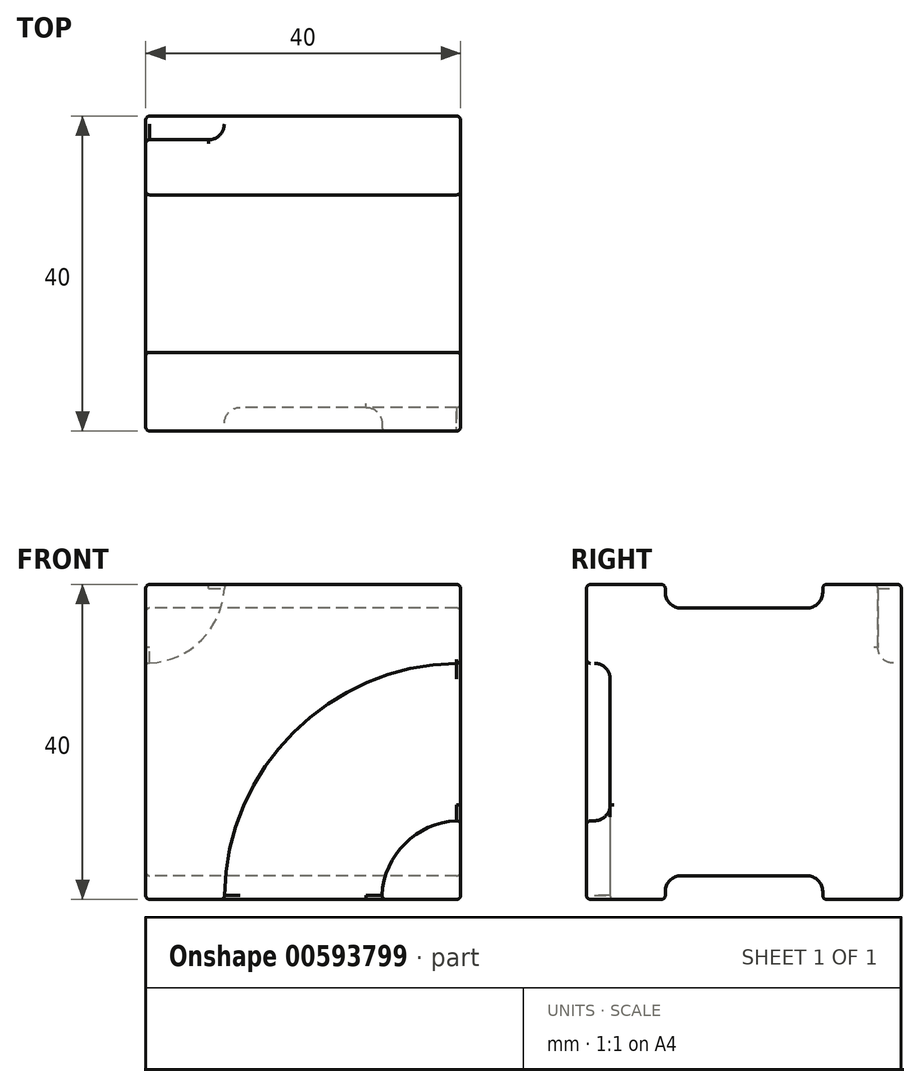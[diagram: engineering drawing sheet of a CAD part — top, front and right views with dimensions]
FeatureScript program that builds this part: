
annotation { "Feature Type Name" : "Feature", "Feature Type Description" : "" }
export const myFeature = defineFeature(function(context is Context, id is Id, definition is map)
    precondition{}
    {
        {
            var Q0;
            Q0=qCreatedBy(makeId("Front.planeOp"),FACE);
            var sketch = newSketch(context, id + "F0", { "sketchPlane" : qUnion([Q0])});
            skLineSegment(sketch, "E0.bottom", {"start": v(20, -20) * mm, "end": v(-20, -20) * mm});
            skLineSegment(sketch, "E0.top", {"start": v(20, 20) * mm, "end": v(-20, 20) * mm});
            skLineSegment(sketch, "E0.left", {"start": v(20, -20) * mm, "end": v(20, 20) * mm});
            skLineSegment(sketch, "E0.right", {"start": v(-20, -20) * mm, "end": v(-20, 20) * mm});
            skPoint(sketch, "E0.middle", {"position": v(0, 0) * mm});
            skSolve(sketch);
        }
        {
            var Q0;
            Q0=makeQuery(id+"F0.imprint","IMPRINT",FACE,{"disambiguationData":[TD([[makeQuery(id+"F0.imprint","IMPRINT",EDGE,{"derivedFrom":sQuery(id+"F0.wireOp",EDGE,"E0.bottom")}),-1.0]])]});
            extrude(context, id + "F1", {"entities" : qUnion([Q0]), "depth" : 40 * mm, "offsetDistance" : 25 * mm, "symmetric" : true});
        }
        {
            var Q0;
            Q0=makeQuery(id+"F1.opExtrude","SWEPT_FACE",FACE,{"disambiguationData":[OSD([sQuery(id+"F0.wireOp",EDGE,"E0.top")])]});
            var sketch = newSketch(context, id + "F2", { "sketchPlane" : qUnion([Q0])});
            skLineSegment(sketch, "E1", {"start": v(34.86, 0) * mm, "end": v(-35.2, 0) * mm, "construction": true});
            skPoint(sketch, "E1.endSnap0", {"position": v(-20, 0) * mm});
            skLineSegment(sketch, "E2.bottom", {"start": v(20, 10) * mm, "end": v(-20, 10) * mm});
            skLineSegment(sketch, "E2.right", {"start": v(-20, 10) * mm, "end": v(-20, 0) * mm});
            skLineSegment(sketch, "E3", {"start": v(20, 10) * mm, "end": v(20, 0) * mm});
            skLineSegment(sketch, "E4.MirrorCS", {"start": v(-20, -10) * mm, "end": v(-20, 0) * mm});
            skLineSegment(sketch, "E5.MirrorCS", {"start": v(20, -10) * mm, "end": v(20, 0) * mm});
            skLineSegment(sketch, "E6.MirrorCS", {"start": v(20, -10) * mm, "end": v(-20, -10) * mm});
            skSolve(sketch);
        }
        {
            var Q0;
            Q0=qSketchRegion(id+"F2",true);
            extrude(context, id + "F3", {"entities" : qUnion([Q0]), "operationType" : NewBodyOperationType.REMOVE, "oppositeDirection" : true, "depth" : 3 * mm, "offsetDistance" : 25 * mm});
        }
        {
            var Q0;
            Q0=makeQuery(id+"F1.opExtrude","SWEPT_FACE",FACE,{"disambiguationData":[OSD([sQuery(id+"F0.wireOp",EDGE,"E0.bottom")])]});
            var sketch = newSketch(context, id + "F4", { "sketchPlane" : qUnion([Q0])});
            skLineSegment(sketch, "E7", {"start": v(31.12, 0) * mm, "end": v(-32.74, 0) * mm, "construction": true});
            skPoint(sketch, "E7.endSnap0", {"position": v(24.5, 0) * mm});
            skLineSegment(sketch, "E8.bottom", {"start": v(20, 10) * mm, "end": v(-20, 10) * mm});
            skLineSegment(sketch, "E8.top", {"start": v(20, -10) * mm, "end": v(-20, -10) * mm});
            skLineSegment(sketch, "E8.left", {"start": v(20, 10) * mm, "end": v(20, -10) * mm});
            skLineSegment(sketch, "E8.right", {"start": v(-20, 10) * mm, "end": v(-20, -10) * mm});
            skSolve(sketch);
        }
        {
            var Q0;
            Q0=qSketchRegion(id+"F4",true);
            extrude(context, id + "F5", {"entities" : qUnion([Q0]), "operationType" : NewBodyOperationType.REMOVE, "oppositeDirection" : true, "depth" : 3 * mm, "offsetDistance" : 25 * mm});
        }
        {
            var Q0;
            Q0=makeQuery(id+"F1.opExtrude","CAP_FACE",FACE,{"disambiguationData":[OSD([sQuery(id+"F0.wireOp",EDGE,"E0.bottom"),sQuery(id+"F0.wireOp",EDGE,"E0.top"),sQuery(id+"F0.wireOp",EDGE,"E0.left"),sQuery(id+"F0.wireOp",EDGE,"E0.right")])],"isStart":false});
            var sketch = newSketch(context, id + "F6", { "sketchPlane" : qUnion([Q0])});
            skArc(sketch, "E9", {"start": v(10, -20) * mm, "mid": v(12.93, -12.93) * mm, "end": v(20, -10) * mm});
            skArc(sketch, "E10.0", {"start": v(-10, -20) * mm, "mid": v(-1.21, 1.21) * mm, "end": v(20, 10) * mm});
            skLineSegment(sketch, "E11", {"start": v(10, -20) * mm, "end": v(-10, -20) * mm});
            skLineSegment(sketch, "E12", {"start": v(20, -10) * mm, "end": v(20, 10) * mm});
            skSolve(sketch);
        }
        {
            var Q0;
            Q0=qSketchRegion(id+"F6",true);
            extrude(context, id + "F7", {"entities" : qUnion([Q0]), "operationType" : NewBodyOperationType.REMOVE, "oppositeDirection" : true, "depth" : 3 * mm, "offsetDistance" : 25 * mm});
        }
        {
            var Q0;
            Q0=makeQuery(id+"F1.opExtrude","CAP_FACE",FACE,{"disambiguationData":[OSD([sQuery(id+"F0.wireOp",EDGE,"E0.bottom"),sQuery(id+"F0.wireOp",EDGE,"E0.top"),sQuery(id+"F0.wireOp",EDGE,"E0.left"),sQuery(id+"F0.wireOp",EDGE,"E0.right")])],"isStart":true});
            var sketch = newSketch(context, id + "F8", { "sketchPlane" : qUnion([Q0])});
            skArc(sketch, "E13", {"start": v(20, 10) * mm, "mid": v(12.93, 12.93) * mm, "end": v(10, 20) * mm});
            skArc(sketch, "E14", {"start": v(20, -10) * mm, "mid": v(-1.21, -1.21) * mm, "end": v(-10, 20) * mm});
            skLineSegment(sketch, "E15", {"start": v(20, -10) * mm, "end": v(20, 10) * mm});
            skLineSegment(sketch, "E16", {"start": v(10, 20) * mm, "end": v(-10, 20) * mm});
            skLineSegment(sketch, "E17", {"start": v(-10, 20) * mm, "end": v(-10, -20) * mm});
            skLineSegment(sketch, "E18", {"start": v(-10, -20) * mm, "end": v(10, -20) * mm});
            skArc(sketch, "E19", {"start": v(10, -20) * mm, "mid": v(12.93, -12.93) * mm, "end": v(20, -10) * mm});
            skSolve(sketch);
        }
        {
            var Q0;
            Q0=makeQuery(id+"F8.imprint","IMPRINT",FACE,{"disambiguationData":[TD([[makeQuery(id+"F8.imprint","IMPRINT",EDGE,{"derivedFrom":sQuery(id+"F8.wireOp",EDGE,"S0vOXXMj-KSPf-uTmC-3DLV-lmScbWxBIAN8")}),1.0]])]});
            var Q1;
            Q1=makeQuery(id+"F8.imprint","IMPRINT",FACE,{"disambiguationData":[TD([[makeQuery(id+"F8.imprint","IMPRINT",EDGE,{"derivedFrom":sQuery(id+"F8.wireOp",EDGE,"E13")}),1.0]])]});
            extrude(context, id + "F9", {"entities" : qUnion([Q0, Q1]), "operationType" : NewBodyOperationType.REMOVE, "oppositeDirection" : true, "depth" : 3 * mm, "offsetDistance" : 25 * mm});
        }
        {
            var Q0;
            Q0=makeQuery(id+"F5.boolean.opBoolean","COPY",EDGE,{"derivedFrom":makeQuery(id+"F5.opExtrude","CAP_EDGE",EDGE,{"disambiguationData":[OSD([sQuery(id+"F4.wireOp",EDGE,"E8.top")])],"isStart":false})});
            var Q1;
            Q1=makeQuery(id+"F5.boolean.opBoolean","COPY",EDGE,{"derivedFrom":makeQuery(id+"F5.opExtrude","CAP_EDGE",EDGE,{"disambiguationData":[OSD([sQuery(id+"F4.wireOp",EDGE,"E8.bottom")])],"isStart":false})});
            var Q2;
            Q2=makeQuery(id+"F7.boolean.opBoolean","COPY",EDGE,{"derivedFrom":makeQuery(id+"F7.opExtrude","CAP_EDGE",EDGE,{"disambiguationData":[OSD([sQuery(id+"F6.wireOp",EDGE,"E10.0")])],"isStart":false})});
            var Q3;
            Q3=makeQuery(id+"F7.boolean.opBoolean","COPY",EDGE,{"derivedFrom":makeQuery(id+"F7.opExtrude","CAP_EDGE",EDGE,{"disambiguationData":[OSD([sQuery(id+"F6.wireOp",EDGE,"E9")])],"isStart":false})});
            var Q4;
            Q4=makeQuery(id+"F9.boolean.opBoolean","COPY",EDGE,{"derivedFrom":makeQuery(id+"F9.opExtrude","CAP_EDGE",EDGE,{"disambiguationData":[OSD([sQuery(id+"F8.wireOp",EDGE,"E17")])],"isStart":false})});
            var Q5;
            Q5=makeQuery(id+"F9.boolean.opBoolean","COPY",EDGE,{"derivedFrom":makeQuery(id+"F9.opExtrude","CAP_EDGE",EDGE,{"disambiguationData":[OSD([sQuery(id+"F8.wireOp",EDGE,"E13")])],"isStart":false})});
            var Q6;
            Q6=makeQuery(id+"F9.boolean.opBoolean","COPY",EDGE,{"derivedFrom":makeQuery(id+"F9.opExtrude","CAP_EDGE",EDGE,{"disambiguationData":[OSD([sQuery(id+"F8.wireOp",EDGE,"E19")])],"isStart":false})});
            var Q7;
            Q7=makeQuery(id+"F3.boolean.opBoolean","COPY",EDGE,{"derivedFrom":makeQuery(id+"F3.opExtrude","CAP_EDGE",EDGE,{"disambiguationData":[OSD([sQuery(id+"F2.wireOp",EDGE,"E6.MirrorCS")])],"isStart":false})});
            var Q8;
            Q8=makeQuery(id+"F3.boolean.opBoolean","COPY",EDGE,{"derivedFrom":makeQuery(id+"F3.opExtrude","CAP_EDGE",EDGE,{"disambiguationData":[OSD([sQuery(id+"F2.wireOp",EDGE,"E2.bottom")])],"isStart":false})});
            var Q9;
            Q9=makeQuery(id+"F9.boolean.opBoolean","COPY",EDGE,{"derivedFrom":makeQuery(id+"F9.opExtrude","CAP_EDGE",EDGE,{"disambiguationData":[OSD([sQuery(id+"F8.wireOp",EDGE,"E14")])],"isStart":false})});
            fillet(context, id + "F10", {"entities" : qUnion([Q0, Q1, Q2, Q3, Q4, Q5, Q6, Q7, Q8, Q9]), "radius" : 2 * mm, "tangentPropagation" : true, "allowEdgeOverflow" : false});
        }
        {
            var Q0;
            {var subQ0=sQuery(id+"F0.wireOp",EDGE,"E0.left");var subQ1=sQuery(id+"F0.wireOp",EDGE,"E0.top");var subQ2=sQuery(id+"F0.wireOp",EDGE,"E0.right");var subQ5=sQuery(id+"F0.wireOp",EDGE,"E0.bottom");Q0=makeQuery(id+"FeEYurADESSjoWS_1.boolean.opBoolean","SPLIT",FACE,{"disambiguationData":[TD([makeQuery(id+"F1.opExtrude","SWEPT_FACE",FACE,{"disambiguationData":[OSD([subQ1])]})])],"derivedFrom":makeQuery(id+"F1.opExtrude","CAP_FACE",FACE,{"disambiguationData":[OSD([subQ5,subQ1,subQ0,subQ2])],"isStart":false})});}
            var Q1;
            Q1=makeQuery(id+"F1.opExtrude","SWEPT_FACE",FACE,{"disambiguationData":[OSD([sQuery(id+"F0.wireOp",EDGE,"E0.right")])]});
            var Q2;
            {var subQ0=sQuery(id+"F0.wireOp",EDGE,"E0.right");var subQ1=sQuery(id+"F0.wireOp",EDGE,"E0.bottom");Q2=makeQuery(id+"FeEYurADESSjoWS_1.boolean.opBoolean","SPLIT",FACE,{"disambiguationData":[TD([makeQuery(id+"FeEYurADESSjoWS_1.opExtrude","SWEPT_FACE",FACE,{"disambiguationData":[OSD([sQuery(id+"F6.wireOp",EDGE,"bcd692f1-bbfa-4d88-a7f8-9c818706eb5d.0")])]})])],"derivedFrom":makeQuery(id+"F1.opExtrude","CAP_FACE",FACE,{"disambiguationData":[OSD([subQ1,sQuery(id+"F0.wireOp",EDGE,"E0.top"),sQuery(id+"F0.wireOp",EDGE,"E0.left"),subQ0])],"isStart":false})});}
            var Q3;
            {var subQ2=sQuery(id+"F0.wireOp",EDGE,"E0.bottom");Q3=makeQuery(id+"F5.boolean.opBoolean","SPLIT",FACE,{"disambiguationData":[TD([makeQuery(id+"F5.opExtrude","SWEPT_FACE",FACE,{"disambiguationData":[OSD([sQuery(id+"F4.wireOp",EDGE,"E8.bottom")])]})])],"derivedFrom":makeQuery(id+"F1.opExtrude","SWEPT_FACE",FACE,{"disambiguationData":[OSD([subQ2])]})});}
            var Q4;
            {var subQ2=sQuery(id+"F0.wireOp",EDGE,"E0.bottom");Q4=makeQuery(id+"F5.boolean.opBoolean","SPLIT",FACE,{"disambiguationData":[TD([makeQuery(id+"F5.opExtrude","SWEPT_FACE",FACE,{"disambiguationData":[OSD([sQuery(id+"F4.wireOp",EDGE,"E8.top")])]})])],"derivedFrom":makeQuery(id+"F1.opExtrude","SWEPT_FACE",FACE,{"disambiguationData":[OSD([subQ2])]})});}
            var Q5;
            {var subQ0=sQuery(id+"F0.wireOp",EDGE,"E0.left");var subQ1=sQuery(id+"F0.wireOp",EDGE,"E0.top");var subQ2=sQuery(id+"F0.wireOp",EDGE,"E0.right");var subQ5=sQuery(id+"F0.wireOp",EDGE,"E0.bottom");Q5=makeQuery(id+"FHPeFrndoI6grQq_1.boolean.opBoolean","SPLIT",FACE,{"disambiguationData":[TD([makeQuery(id+"F1.opExtrude","SWEPT_FACE",FACE,{"disambiguationData":[OSD([subQ1])]})])],"derivedFrom":makeQuery(id+"F1.opExtrude","CAP_FACE",FACE,{"disambiguationData":[OSD([subQ5,subQ1,subQ0,subQ2])],"isStart":true})});}
            var Q6;
            {var subQ0=sQuery(id+"F0.wireOp",EDGE,"E0.left");var subQ1=sQuery(id+"F0.wireOp",EDGE,"E0.bottom");Q6=makeQuery(id+"FHPeFrndoI6grQq_1.boolean.opBoolean","SPLIT",FACE,{"disambiguationData":[TD([makeQuery(id+"FHPeFrndoI6grQq_1.opExtrude","SWEPT_FACE",FACE,{"disambiguationData":[OSD([sQuery(id+"FpqyqDqQfxwQ36t_1.wireOp",EDGE,"11a5f918-374d-4318-88e4-5ad5a2d605e7.0")])]})])],"derivedFrom":makeQuery(id+"F1.opExtrude","CAP_FACE",FACE,{"disambiguationData":[OSD([subQ1,sQuery(id+"F0.wireOp",EDGE,"E0.top"),subQ0,sQuery(id+"F0.wireOp",EDGE,"E0.right")])],"isStart":true})});}
            var Q7;
            {var subQ0=sQuery(id+"F0.wireOp",EDGE,"E0.left");Q7=makeQuery(id+"FhphGXGLthVadN0_1.boolean.opBoolean","SPLIT",FACE,{"disambiguationData":[TD([makeQuery(id+"F5.boolean.opBoolean","COPY",FACE,{"derivedFrom":makeQuery(id+"F5.opExtrude","SWEPT_FACE",FACE,{"disambiguationData":[OSD([sQuery(id+"F4.wireOp",EDGE,"E8.top")])]})})])],"derivedFrom":makeQuery(id+"F1.opExtrude","SWEPT_FACE",FACE,{"disambiguationData":[OSD([subQ0])]})});}
            var Q8;
            {var subQ0=sQuery(id+"F0.wireOp",EDGE,"E0.top");var subQ2=sQuery(id+"F0.wireOp",EDGE,"E0.left");Q8=makeQuery(id+"FhphGXGLthVadN0_1.boolean.opBoolean","SPLIT",FACE,{"disambiguationData":[TD([makeQuery(id+"F1.opExtrude","SWEPT_FACE",FACE,{"disambiguationData":[OSD([subQ0])]})])],"derivedFrom":makeQuery(id+"F1.opExtrude","SWEPT_FACE",FACE,{"disambiguationData":[OSD([subQ2])]})});}
            var Q9;
            {var subQ0=sQuery(id+"F0.wireOp",EDGE,"E0.left");Q9=makeQuery(id+"FhphGXGLthVadN0_1.boolean.opBoolean","SPLIT",FACE,{"disambiguationData":[TD([makeQuery(id+"F5.boolean.opBoolean","COPY",FACE,{"derivedFrom":makeQuery(id+"F5.opExtrude","SWEPT_FACE",FACE,{"disambiguationData":[OSD([sQuery(id+"F4.wireOp",EDGE,"E8.bottom")])]})})])],"derivedFrom":makeQuery(id+"F1.opExtrude","SWEPT_FACE",FACE,{"disambiguationData":[OSD([subQ0])]})});}
            var Q10;
            {var subQ1=sQuery(id+"F0.wireOp",EDGE,"E0.left");var subQ2=sQuery(id+"F0.wireOp",EDGE,"E0.top");Q10=makeQuery(id+"F3.boolean.opBoolean","SPLIT",FACE,{"disambiguationData":[TD([makeQuery(id+"F1.opExtrude","SWEPT_FACE",FACE,{"disambiguationData":[OSD([subQ1])]})])],"derivedFrom":makeQuery(id+"F1.opExtrude","SWEPT_FACE",FACE,{"disambiguationData":[OSD([subQ2])]})});}
            var Q11;
            {var subQ0=sQuery(id+"F0.wireOp",EDGE,"E0.right");var subQ2=sQuery(id+"F0.wireOp",EDGE,"E0.top");Q11=makeQuery(id+"F3.boolean.opBoolean","SPLIT",FACE,{"disambiguationData":[TD([makeQuery(id+"F1.opExtrude","SWEPT_FACE",FACE,{"disambiguationData":[OSD([subQ0])]})])],"derivedFrom":makeQuery(id+"F1.opExtrude","SWEPT_FACE",FACE,{"disambiguationData":[OSD([subQ2])]})});}
            var Q12;
            Q12=makeQuery(id+"FhphGXGLthVadN0_1.boolean.opBoolean","COPY",EDGE,{"derivedFrom":makeQuery(id+"FhphGXGLthVadN0_1.opExtrude","CAP_EDGE",EDGE,{"disambiguationData":[OSD([sQuery(id+"F0.wireOp",EDGE,"E0.left"),sQuery(id+"FpqyqDqQfxwQ36t_1.wireOp",EDGE,"0759713e-e7df-4183-9224-c0852353a63a.0"),sQuery(id+"FpqyqDqQfxwQ36t_1.wireOp",EDGE,"0759713e-e7df-4183-9224-c0852353a63a.1"),sQuery(id+"FpqyqDqQfxwQ36t_1.wireOp",EDGE,"11a5f918-374d-4318-88e4-5ad5a2d605e7.0"),sQuery(id+"FpqyqDqQfxwQ36t_1.wireOp",EDGE,"11a5f918-374d-4318-88e4-5ad5a2d605e7.1"),sQuery(id+"FpqyqDqQfxwQ36t_1.wireOp",EDGE,"zKdxWZJF-1CZ5-eTvP-v24i-ATzPNmKQrU5U"),sQuery(id+"FpqyqDqQfxwQ36t_1.wireOp",EDGE,"wMGJVRBH-eHaP-nP1o-tBN4-yRPVe8nUY65C"),sQuery(id+"FpqyqDqQfxwQ36t_1.wireOp",EDGE,"61521492-cf4c-4c9f-b70c-34a3293a7591.filletArc"),sQuery(id+"FpqyqDqQfxwQ36t_1.wireOp",EDGE,"dc6e6eda-5071-4c0c-bfe8-26dd1b046b33.filletArc")])],"isStart":false})});
            var Q13;
            Q13=makeQuery(id+"FhphGXGLthVadN0_1.boolean.opBoolean","COPY",EDGE,{"derivedFrom":makeQuery(id+"FhphGXGLthVadN0_1.opExtrude","CAP_EDGE",EDGE,{"disambiguationData":[OSD([sQuery(id+"FWu8rZYhLeN4OZv_1.wireOp",EDGE,"ZuCWKp1C-7wbl-hlMd-doiS-uhh4Hec1rI5d")])],"isStart":false})});
            fillet(context, id + "F11", {"entities" : qUnion([Q0, Q1, Q2, Q3, Q4, Q5, Q6, Q7, Q8, Q9, Q10, Q11, Q12, Q13]), "radius" : 0.5 * mm, "tangentPropagation" : true, "allowEdgeOverflow" : false});
        }
    });
